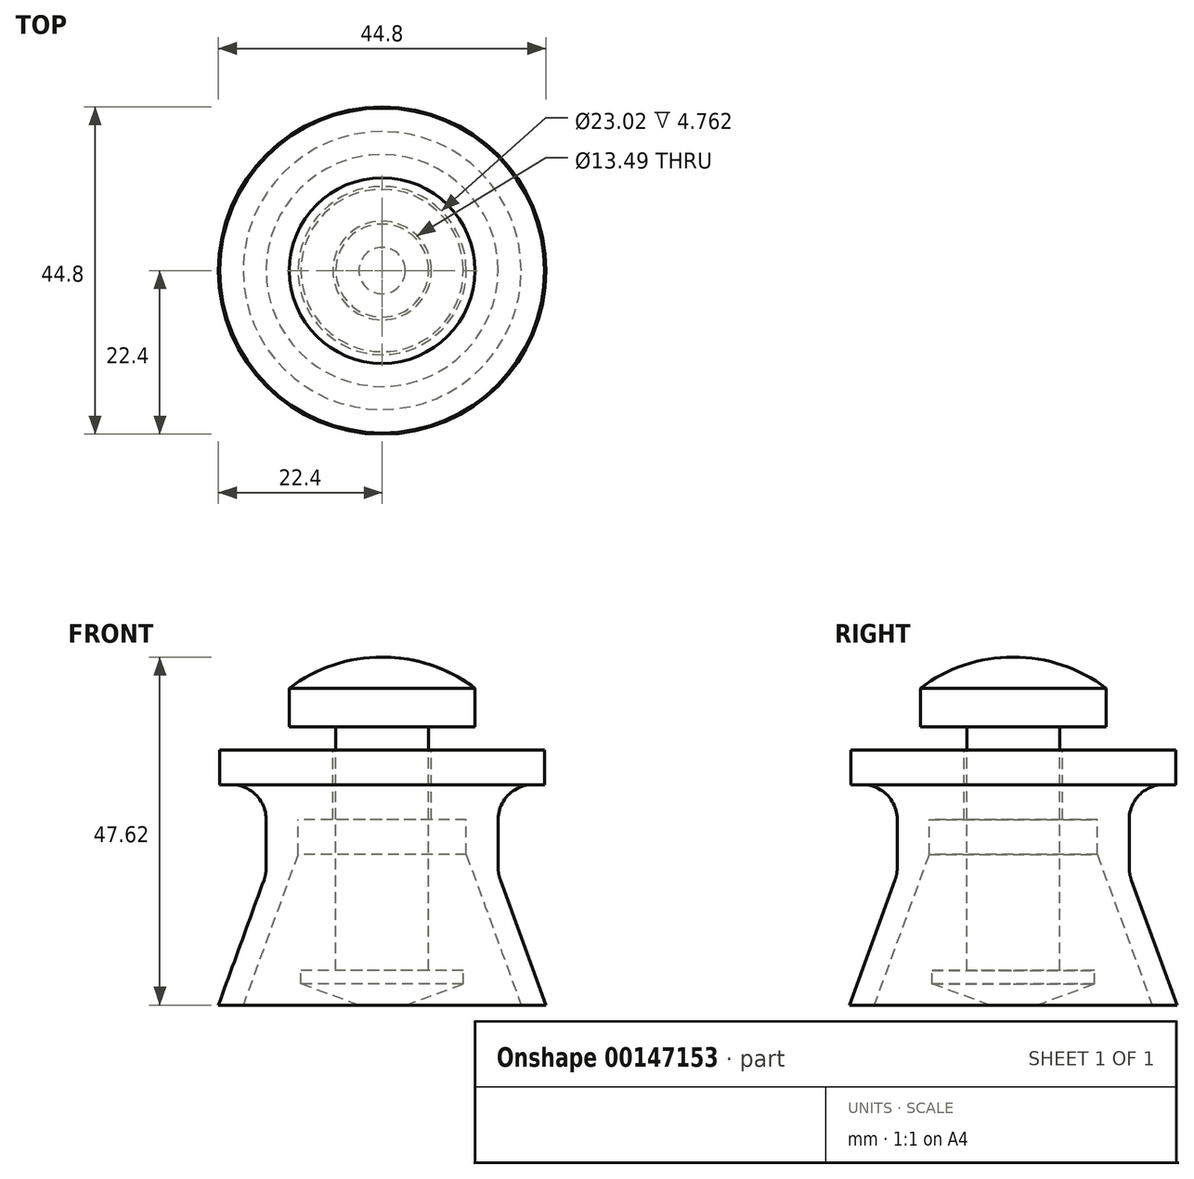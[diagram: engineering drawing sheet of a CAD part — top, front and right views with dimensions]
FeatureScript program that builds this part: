
annotation { "Feature Type Name" : "Feature", "Feature Type Description" : "" }
export const myFeature = defineFeature(function(context is Context, id is Id, definition is map)
    precondition{}
    {
        {
            var Q0;
            Q0=qCreatedBy(makeId("Front.planeOp"),FACE);
            var sketch = newSketch(context, id + "F0", { "sketchPlane" : qUnion([Q0])});
            skLineSegment(sketch, "E0", {"start": v(0, 0) * mm, "end": v(3.17, 0) * mm});
            skLineSegment(sketch, "E1", {"start": v(3.17, 0) * mm, "end": v(11.11, 2.89) * mm});
            skLineSegment(sketch, "E2", {"start": v(11.11, 2.89) * mm, "end": v(11.11, 4.76) * mm});
            skCircle(sketch, "E3", {"center": v(0, 21.28) * mm, "radius": 21.08 * mm, "construction": true});
            skLineSegment(sketch, "E4", {"start": v(0, 0) * mm, "end": v(0, 47.62) * mm});
            skLineSegment(sketch, "E5", {"start": v(0, 0) * mm, "end": v(0, -15.55) * mm, "construction": true});
            skLineSegment(sketch, "E6", {"start": v(6.35, 38.1) * mm, "end": v(6.35, 4.76) * mm});
            skLineSegment(sketch, "E7", {"start": v(6.35, 4.76) * mm, "end": v(11.11, 4.76) * mm});
            skLineSegment(sketch, "E8", {"start": v(-22.4, 0) * mm, "end": v(-19.02, 0) * mm});
            skLineSegment(sketch, "E9", {"start": v(-19.02, 0) * mm, "end": v(-11.5, 20.64) * mm});
            skLineSegment(sketch, "E10", {"start": v(-11.5, 20.64) * mm, "end": v(-11.5, 25.4) * mm});
            skLineSegment(sketch, "E11", {"start": v(-11.5, 25.4) * mm, "end": v(-6.75, 25.4) * mm});
            skLineSegment(sketch, "E12", {"start": v(-6.75, 25.4) * mm, "end": v(-6.75, 34.92) * mm});
            skLineSegment(sketch, "E13", {"start": v(-15.88, 30.16) * mm, "end": v(-15.88, 17.93) * mm});
            skLineSegment(sketch, "E14", {"start": v(-15.88, 17.93) * mm, "end": v(-22.4, 0) * mm});
            skPoint(sketch, "E15.end.orphan", {"position": v(-20.09, 53.97) * mm});
            skPoint(sketch, "E16.end.orphan", {"position": v(-11.5, 34.92) * mm});
            skLineSegment(sketch, "E17", {"start": v(-6.75, 34.92) * mm, "end": v(-22.23, 34.92) * mm});
            skLineSegment(sketch, "E18", {"start": v(-15.88, 30.16) * mm, "end": v(-22.23, 30.16) * mm});
            skLineSegment(sketch, "E19", {"start": v(-22.23, 34.92) * mm, "end": v(-22.23, 30.16) * mm});
            skLineSegment(sketch, "E20", {"start": v(6.35, 38.1) * mm, "end": v(12.7, 38.1) * mm});
            skLineSegment(sketch, "E21", {"start": v(12.7, 43.37) * mm, "end": v(12.7, 38.1) * mm});
            skArc(sketch, "E22", {"start": v(12.7, 43.37) * mm, "mid": v(6.7, 46.53) * mm, "end": v(0, 47.62) * mm});
            skSolve(sketch);
        }
        {
            var Q0;
            Q0=qSketchRegion(id+"F0",true);
            var Q1;
            Q1=sQuery(id+"F0.wireOp",EDGE,"E5");
            revolve(context, id + "F1", {"entities" : qUnion([Q0]), "axis" : qUnion([Q1]), "revolveType" : RevolveType.FULL});
        }
        {
            var Q0;
            Q0=makeQuery(id+"F1.opRevolve","SWEPT_EDGE",EDGE,{"disambiguationData":[OSD([sQuery(id+"F0.wireOp",EDGE,"E13"),sQuery(id+"F0.wireOp",EDGE,"E18")])]});
            var Q1;
            Q1=makeQuery(id+"F1.opRevolve","SWEPT_EDGE",EDGE,{"disambiguationData":[OSD([sQuery(id+"F0.wireOp",EDGE,"E13"),sQuery(id+"F0.wireOp",EDGE,"E14")])]});
            fillet(context, id + "F2", {"entities" : qUnion([Q0, Q1]), "radius" : 4.76 * mm, "tangentPropagation" : true, "allowEdgeOverflow" : false});
        }
    });
